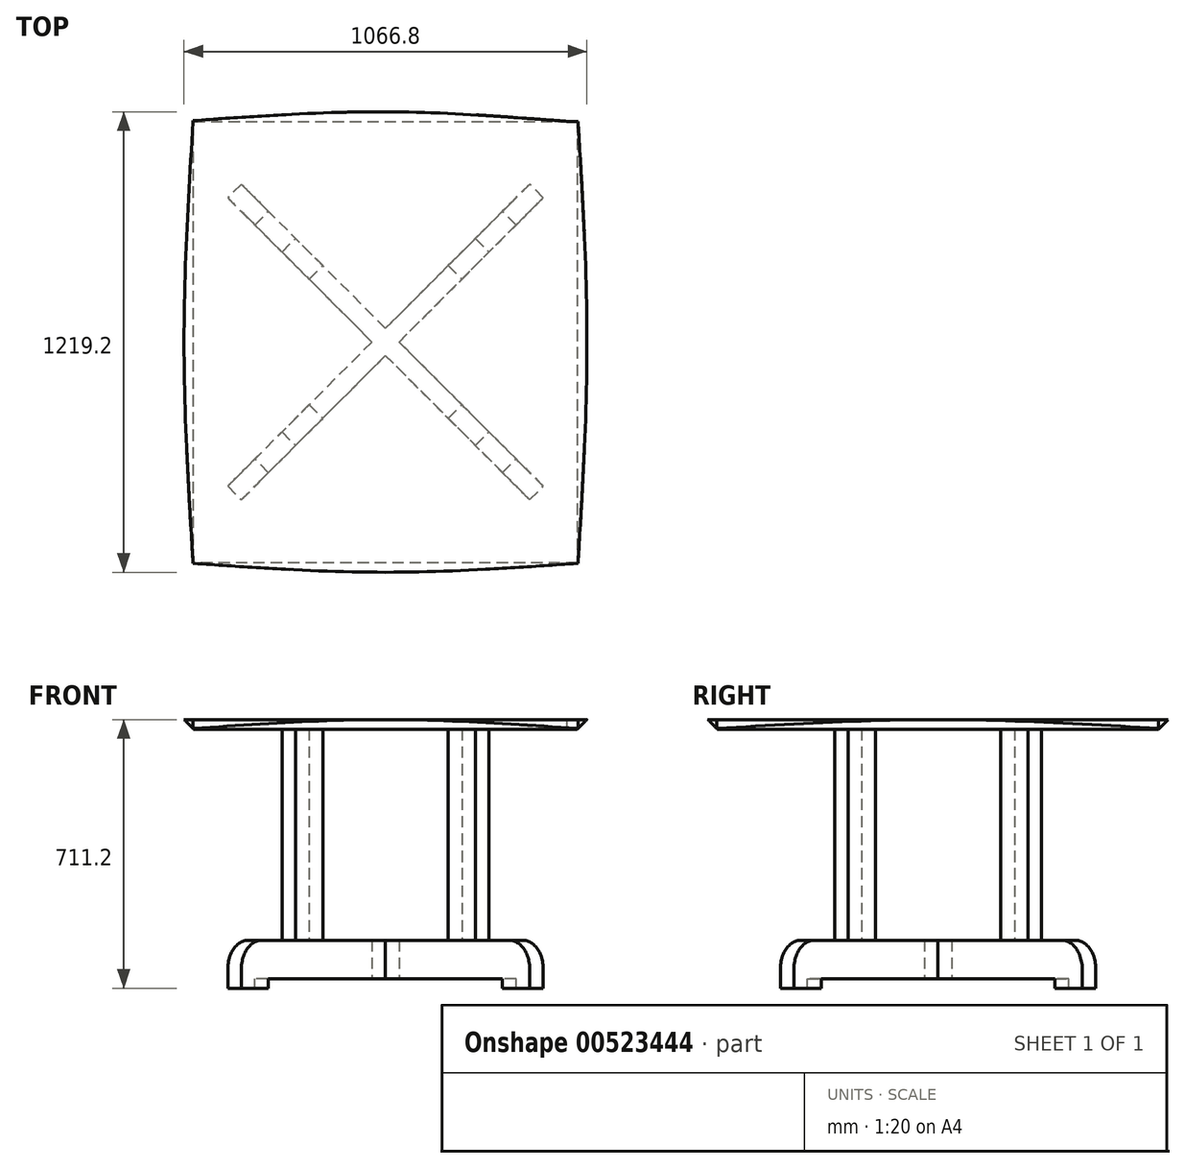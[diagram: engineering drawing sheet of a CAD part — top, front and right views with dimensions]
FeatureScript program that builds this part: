
annotation { "Feature Type Name" : "Feature", "Feature Type Description" : "" }
export const myFeature = defineFeature(function(context is Context, id is Id, definition is map)
    precondition{}
    {
        {
            var Q0;
            Q0=qCreatedBy(makeId("Top.planeOp"),FACE);
            var sketch = newSketch(context, id + "F0", { "sketchPlane" : qUnion([Q0])});
            skLineSegment(sketch, "E0.bottom", {"start": v(-533.4, 609.6) * mm, "end": v(533.4, 609.6) * mm});
            skLineSegment(sketch, "E0.top", {"start": v(-533.4, -609.6) * mm, "end": v(533.4, -609.6) * mm});
            skLineSegment(sketch, "E0.left", {"start": v(-533.4, 609.6) * mm, "end": v(-533.4, -609.6) * mm});
            skLineSegment(sketch, "E0.right", {"start": v(533.4, 609.6) * mm, "end": v(533.4, -609.6) * mm});
            skPoint(sketch, "E1.visualSharp", {"position": v(-533.4, 609.6) * mm});
            skPoint(sketch, "E2.visualSharp", {"position": v(533.4, 609.6) * mm});
            skPoint(sketch, "E3.visualSharp", {"position": v(533.4, -609.6) * mm});
            skPoint(sketch, "E4.visualSharp", {"position": v(-533.4, -609.6) * mm});
            skSolve(sketch);
        }
        {
            var Q0;
            Q0=makeQuery(id+"F0.imprint","IMPRINT",FACE,{"disambiguationData":[TD([[makeQuery(id+"F0.imprint","IMPRINT",EDGE,{"derivedFrom":sQuery(id+"F0.wireOp",EDGE,"E0.bottom")}),-1.0]])]});
            extrude(context, id + "F1", {"entities" : qUnion([Q0]), "depth" : 25.4 * mm, "offsetDistance" : 25.4 * mm});
        }
        {
            var Q0;
            Q0=makeQuery(id+"F1.opExtrude","CAP_EDGE",EDGE,{"disambiguationData":[OSD([sQuery(id+"F0.wireOp",EDGE,"E0.right")])],"isStart":true});
            var Q1;
            Q1=makeQuery(id+"F1.opExtrude","CAP_EDGE",EDGE,{"disambiguationData":[OSD([sQuery(id+"F0.wireOp",EDGE,"E0.top")])],"isStart":true});
            var Q2;
            Q2=makeQuery(id+"F1.opExtrude","CAP_EDGE",EDGE,{"disambiguationData":[OSD([sQuery(id+"F0.wireOp",EDGE,"E0.left")])],"isStart":true});
            var Q3;
            Q3=makeQuery(id+"F1.opExtrude","CAP_EDGE",EDGE,{"disambiguationData":[OSD([sQuery(id+"F0.wireOp",EDGE,"E0.bottom")])],"isStart":true});
            chamfer(context, id + "F2", {"entities" : qUnion([Q0, Q1, Q2, Q3]), "width" : 25.4 * mm, "tangentPropagation" : true});
        }
        {
            var Q0;
            Q0=makeQuery(id+"F1.opExtrude","CAP_FACE",FACE,{"disambiguationData":[OSD([sQuery(id+"F0.wireOp",EDGE,"E0.bottom"),sQuery(id+"F0.wireOp",EDGE,"E0.top"),sQuery(id+"F0.wireOp",EDGE,"E0.left"),sQuery(id+"F0.wireOp",EDGE,"E0.right")])],"isStart":false});
            var sketch = newSketch(context, id + "F3", { "sketchPlane" : qUnion([Q0])});
            skLineSegment(sketch, "E5.0", {"start": v(-533.4, -584.2) * mm, "end": v(533.4, -584.2) * mm});
            skLineSegment(sketch, "E5.1", {"start": v(508, 609.6) * mm, "end": v(508, -609.6) * mm});
            skLineSegment(sketch, "E6.0", {"start": v(-533.4, 584.2) * mm, "end": v(533.4, 584.2) * mm});
            skLineSegment(sketch, "E6.1", {"start": v(-508, 609.6) * mm, "end": v(-508, -609.6) * mm});
            skLineSegment(sketch, "E7.0", {"start": v(-533.4, -609.6) * mm, "end": v(533.4, -609.6) * mm});
            skLineSegment(sketch, "E8.0", {"start": v(-533.4, 609.6) * mm, "end": v(-533.4, -609.6) * mm});
            skLineSegment(sketch, "E9.0", {"start": v(-533.4, 609.6) * mm, "end": v(533.4, 609.6) * mm});
            skLineSegment(sketch, "E10.0", {"start": v(533.4, 609.6) * mm, "end": v(533.4, -609.6) * mm});
            skFitSpline(sketch, "E11", {"points": [v(508, -609.6) * mm, v(533.4, 0) * mm, v(508, 609.6) * mm], "startDerivative": vector(76.2, 1219.2) * mm, "endDerivative": vector(-76.2, 1219.2) * mm});
            skFitSpline(sketch, "E12", {"points": [v(-508, -609.6) * mm, v(-533.4, 0) * mm, v(-508, 609.6) * mm], "startDerivative": vector(-76.2, 1219.2) * mm, "endDerivative": vector(76.2, 1219.2) * mm});
            skFitSpline(sketch, "E13", {"points": [v(-533.4, -584.2) * mm, v(0, -609.6) * mm, v(533.4, -584.2) * mm], "startDerivative": vector(1066.8, -76.2) * mm, "endDerivative": vector(1066.8, 76.2) * mm});
            skFitSpline(sketch, "E14", {"points": [v(-533.4, 584.2) * mm, v(0, 609.6) * mm, v(480.85, 584.2) * mm], "startDerivative": vector(1066.8, 76.2) * mm, "endDerivative": vector(1066.8, -76.2) * mm});
            skSolve(sketch);
        }
        {
            var Q0;
            {var subQ0=sQuery(id+"F3.wireOp",EDGE,"E7.0");var subQ3=sQuery(id+"F3.wireOp",EDGE,"E13");var subQ5=makeQuery(id+"F3.imprint","INTERSECT",VERTEX,{"derivedFrom":[subQ0,subQ3]});Q0=makeQuery(id+"F3.imprint","IMPRINT",FACE,{"disambiguationData":[TD([[makeQuery(id+"F3.imprint","IMPRINT",EDGE,{"disambiguationData":[TD([[subQ5,1.0]])],"derivedFrom":subQ3}),-1.0]])]});}
            var Q1;
            {var subQ0=sQuery(id+"F3.wireOp",EDGE,"E8.0");var subQ1=sQuery(id+"F3.wireOp",EDGE,"E7.0");var subQ2=makeQuery(id+"F3.imprint","INTERSECT",VERTEX,{"derivedFrom":[subQ1,subQ0]});Q1=makeQuery(id+"F3.imprint","IMPRINT",FACE,{"disambiguationData":[TD([[makeQuery(id+"F3.imprint","IMPRINT",EDGE,{"disambiguationData":[TD([[subQ2,-1.0]])],"derivedFrom":subQ1}),1.0]])]});}
            var Q2;
            {var subQ0=sQuery(id+"F3.wireOp",EDGE,"E8.0");var subQ3=sQuery(id+"F3.wireOp",EDGE,"E12");var subQ5=makeQuery(id+"F3.imprint","INTERSECT",VERTEX,{"derivedFrom":[subQ0,subQ3]});Q2=makeQuery(id+"F3.imprint","IMPRINT",FACE,{"disambiguationData":[TD([[makeQuery(id+"F3.imprint","IMPRINT",EDGE,{"disambiguationData":[TD([[subQ5,1.0]])],"derivedFrom":subQ3}),1.0]])]});}
            var Q3;
            {var subQ0=sQuery(id+"F3.wireOp",EDGE,"E8.0");var subQ3=sQuery(id+"F3.wireOp",EDGE,"E12");var subQ5=makeQuery(id+"F3.imprint","INTERSECT",VERTEX,{"derivedFrom":[subQ0,subQ3]});Q3=makeQuery(id+"F3.imprint","IMPRINT",FACE,{"disambiguationData":[TD([[makeQuery(id+"F3.imprint","IMPRINT",EDGE,{"disambiguationData":[TD([[subQ5,-1.0]])],"derivedFrom":subQ3}),1.0]])]});}
            var Q4;
            {var subQ0=sQuery(id+"F3.wireOp",EDGE,"E9.0");var subQ1=sQuery(id+"F3.wireOp",EDGE,"E8.0");var subQ2=makeQuery(id+"F3.imprint","INTERSECT",VERTEX,{"derivedFrom":[subQ1,subQ0]});Q4=makeQuery(id+"F3.imprint","IMPRINT",FACE,{"disambiguationData":[TD([[makeQuery(id+"F3.imprint","IMPRINT",EDGE,{"disambiguationData":[TD([[subQ2,-1.0]])],"derivedFrom":subQ1}),1.0]])]});}
            var Q5;
            {var subQ0=sQuery(id+"F3.wireOp",EDGE,"E9.0");var subQ3=sQuery(id+"F3.wireOp",EDGE,"E14");var subQ5=makeQuery(id+"F3.imprint","INTERSECT",VERTEX,{"derivedFrom":[subQ0,subQ3]});Q5=makeQuery(id+"F3.imprint","IMPRINT",FACE,{"disambiguationData":[TD([[makeQuery(id+"F3.imprint","IMPRINT",EDGE,{"disambiguationData":[TD([[subQ5,1.0]])],"derivedFrom":subQ3}),1.0]])]});}
            var Q6;
            {var subQ0=sQuery(id+"F3.wireOp",EDGE,"E9.0");var subQ3=sQuery(id+"F3.wireOp",EDGE,"E14");var subQ5=makeQuery(id+"F3.imprint","INTERSECT",VERTEX,{"derivedFrom":[subQ0,subQ3]});Q6=makeQuery(id+"F3.imprint","IMPRINT",FACE,{"disambiguationData":[TD([[makeQuery(id+"F3.imprint","IMPRINT",EDGE,{"disambiguationData":[TD([[subQ5,-1.0]])],"derivedFrom":subQ3}),1.0]])]});}
            var Q7;
            {var subQ0=sQuery(id+"F3.wireOp",EDGE,"E10.0");var subQ1=sQuery(id+"F3.wireOp",EDGE,"E9.0");var subQ2=makeQuery(id+"F3.imprint","INTERSECT",VERTEX,{"derivedFrom":[subQ1,subQ0]});Q7=makeQuery(id+"F3.imprint","IMPRINT",FACE,{"disambiguationData":[TD([[makeQuery(id+"F3.imprint","IMPRINT",EDGE,{"disambiguationData":[TD([[subQ2,1.0]])],"derivedFrom":subQ1}),-1.0]])]});}
            var Q8;
            {var subQ0=sQuery(id+"F3.wireOp",EDGE,"E10.0");var subQ3=sQuery(id+"F3.wireOp",EDGE,"E11");var subQ5=makeQuery(id+"F3.imprint","INTERSECT",VERTEX,{"derivedFrom":[subQ0,subQ3]});Q8=makeQuery(id+"F3.imprint","IMPRINT",FACE,{"disambiguationData":[TD([[makeQuery(id+"F3.imprint","IMPRINT",EDGE,{"disambiguationData":[TD([[subQ5,-1.0]])],"derivedFrom":subQ3}),-1.0]])]});}
            var Q9;
            {var subQ0=sQuery(id+"F3.wireOp",EDGE,"E10.0");var subQ3=sQuery(id+"F3.wireOp",EDGE,"E11");var subQ5=makeQuery(id+"F3.imprint","INTERSECT",VERTEX,{"derivedFrom":[subQ0,subQ3]});Q9=makeQuery(id+"F3.imprint","IMPRINT",FACE,{"disambiguationData":[TD([[makeQuery(id+"F3.imprint","IMPRINT",EDGE,{"disambiguationData":[TD([[subQ5,1.0]])],"derivedFrom":subQ3}),-1.0]])]});}
            var Q10;
            {var subQ0=sQuery(id+"F3.wireOp",EDGE,"E10.0");var subQ1=sQuery(id+"F3.wireOp",EDGE,"E7.0");var subQ2=makeQuery(id+"F3.imprint","INTERSECT",VERTEX,{"derivedFrom":[subQ1,subQ0]});Q10=makeQuery(id+"F3.imprint","IMPRINT",FACE,{"disambiguationData":[TD([[makeQuery(id+"F3.imprint","IMPRINT",EDGE,{"disambiguationData":[TD([[subQ2,1.0]])],"derivedFrom":subQ1}),1.0]])]});}
            var Q11;
            {var subQ0=sQuery(id+"F3.wireOp",EDGE,"E7.0");var subQ3=sQuery(id+"F3.wireOp",EDGE,"E13");var subQ5=makeQuery(id+"F3.imprint","INTERSECT",VERTEX,{"derivedFrom":[subQ0,subQ3]});Q11=makeQuery(id+"F3.imprint","IMPRINT",FACE,{"disambiguationData":[TD([[makeQuery(id+"F3.imprint","IMPRINT",EDGE,{"disambiguationData":[TD([[subQ5,-1.0]])],"derivedFrom":subQ3}),-1.0]])]});}
            var Q12;
            {var subQ1=sQuery(id+"F3.wireOp",EDGE,"E6.0");var subQ3=sQuery(id+"F3.wireOp",EDGE,"E11");var subQ4=makeQuery(id+"F3.imprint","INTERSECT",VERTEX,{"derivedFrom":[subQ1,subQ3]});Q12=makeQuery(id+"F3.imprint","IMPRINT",FACE,{"disambiguationData":[TD([[makeQuery(id+"F3.imprint","IMPRINT",EDGE,{"disambiguationData":[TD([[subQ4,-1.0]])],"derivedFrom":subQ3}),-1.0]])]});}
            var Q13;
            {var subQ1=sQuery(id+"F3.wireOp",EDGE,"E5.1");var subQ3=sQuery(id+"F3.wireOp",EDGE,"E14");var subQ4=makeQuery(id+"F3.imprint","INTERSECT",VERTEX,{"derivedFrom":[subQ1,subQ3]});Q13=makeQuery(id+"F3.imprint","IMPRINT",FACE,{"disambiguationData":[TD([[makeQuery(id+"F3.imprint","IMPRINT",EDGE,{"disambiguationData":[TD([[subQ4,-1.0]])],"derivedFrom":subQ3}),1.0]])]});}
            var Q14;
            {var subQ1=sQuery(id+"F3.wireOp",EDGE,"E5.0");var subQ3=sQuery(id+"F3.wireOp",EDGE,"E11");var subQ4=makeQuery(id+"F3.imprint","INTERSECT",VERTEX,{"derivedFrom":[subQ1,subQ3]});Q14=makeQuery(id+"F3.imprint","IMPRINT",FACE,{"disambiguationData":[TD([[makeQuery(id+"F3.imprint","IMPRINT",EDGE,{"disambiguationData":[TD([[subQ4,1.0]])],"derivedFrom":subQ3}),-1.0]])]});}
            var Q15;
            {var subQ1=sQuery(id+"F3.wireOp",EDGE,"E5.1");var subQ3=sQuery(id+"F3.wireOp",EDGE,"E13");var subQ4=makeQuery(id+"F3.imprint","INTERSECT",VERTEX,{"derivedFrom":[subQ1,subQ3]});Q15=makeQuery(id+"F3.imprint","IMPRINT",FACE,{"disambiguationData":[TD([[makeQuery(id+"F3.imprint","IMPRINT",EDGE,{"disambiguationData":[TD([[subQ4,-1.0]])],"derivedFrom":subQ3}),-1.0]])]});}
            var Q16;
            {var subQ1=sQuery(id+"F3.wireOp",EDGE,"E5.0");var subQ3=sQuery(id+"F3.wireOp",EDGE,"E12");var subQ4=makeQuery(id+"F3.imprint","INTERSECT",VERTEX,{"derivedFrom":[subQ1,subQ3]});Q16=makeQuery(id+"F3.imprint","IMPRINT",FACE,{"disambiguationData":[TD([[makeQuery(id+"F3.imprint","IMPRINT",EDGE,{"disambiguationData":[TD([[subQ4,1.0]])],"derivedFrom":subQ3}),1.0]])]});}
            var Q17;
            {var subQ1=sQuery(id+"F3.wireOp",EDGE,"E6.1");var subQ3=sQuery(id+"F3.wireOp",EDGE,"E13");var subQ4=makeQuery(id+"F3.imprint","INTERSECT",VERTEX,{"derivedFrom":[subQ1,subQ3]});Q17=makeQuery(id+"F3.imprint","IMPRINT",FACE,{"disambiguationData":[TD([[makeQuery(id+"F3.imprint","IMPRINT",EDGE,{"disambiguationData":[TD([[subQ4,1.0]])],"derivedFrom":subQ3}),-1.0]])]});}
            var Q18;
            {var subQ1=sQuery(id+"F3.wireOp",EDGE,"E6.1");var subQ3=sQuery(id+"F3.wireOp",EDGE,"E14");var subQ4=makeQuery(id+"F3.imprint","INTERSECT",VERTEX,{"derivedFrom":[subQ1,subQ3]});Q18=makeQuery(id+"F3.imprint","IMPRINT",FACE,{"disambiguationData":[TD([[makeQuery(id+"F3.imprint","IMPRINT",EDGE,{"disambiguationData":[TD([[subQ4,1.0]])],"derivedFrom":subQ3}),1.0]])]});}
            var Q19;
            {var subQ1=sQuery(id+"F3.wireOp",EDGE,"E6.0");var subQ3=sQuery(id+"F3.wireOp",EDGE,"E12");var subQ4=makeQuery(id+"F3.imprint","INTERSECT",VERTEX,{"derivedFrom":[subQ1,subQ3]});Q19=makeQuery(id+"F3.imprint","IMPRINT",FACE,{"disambiguationData":[TD([[makeQuery(id+"F3.imprint","IMPRINT",EDGE,{"disambiguationData":[TD([[subQ4,-1.0]])],"derivedFrom":subQ3}),1.0]])]});}
            var Q20;
            {var subQ1=sQuery(id+"F3.wireOp",EDGE,"E5.1");var subQ3=sQuery(id+"F3.wireOp",EDGE,"E6.0");var subQ4=makeQuery(id+"F3.imprint","INTERSECT",VERTEX,{"derivedFrom":[subQ1,subQ3]});Q20=makeQuery(id+"F3.imprint","IMPRINT",FACE,{"disambiguationData":[TD([[makeQuery(id+"F3.imprint","IMPRINT",EDGE,{"disambiguationData":[TD([[subQ4,-1.0]])],"derivedFrom":subQ3}),1.0]])]});}
            extrude(context, id + "F4", {"entities" : qUnion([Q0, Q1, Q2, Q3, Q4, Q5, Q6, Q7, Q8, Q9, Q10, Q11, Q12, Q13, Q14, Q15, Q16, Q17, Q18, Q19, Q20]), "operationType" : NewBodyOperationType.REMOVE, "oppositeDirection" : true, "depth" : 25.4 * mm, "offsetDistance" : 25.4 * mm});
        }
        {
            var Q0;
            Q0=makeQuery(id+"F1.opExtrude","CAP_FACE",FACE,{"disambiguationData":[OSD([sQuery(id+"F0.wireOp",EDGE,"E0.bottom"),sQuery(id+"F0.wireOp",EDGE,"E0.top"),sQuery(id+"F0.wireOp",EDGE,"E0.left"),sQuery(id+"F0.wireOp",EDGE,"E0.right")])],"isStart":false});
            cPlane(context, id + "F5", {"entities" : qUnion([Q0]), "cplaneType" : CPlaneType.OFFSET, "offset" : 711.2 * mm, "oppositeDirection" : true, "width" : 152.4 * mm, "height" : 152.4 * mm});
        }
        {
            var Q0;
            Q0=qCreatedBy(id+"F5.planeOp",FACE);
            var sketch = newSketch(context, id + "F6", { "sketchPlane" : qUnion([Q0])});
            skFitSpline(sketch, "E15.0.0", {"points": [v(-533.4, -584.2) * mm, v(-355.6, -596.9) * mm, v(0, -622.3) * mm, v(355.6, -596.9) * mm, v(533.4, -584.2) * mm]});
            skFitSpline(sketch, "E15.0.1", {"points": [v(508, -609.6) * mm, v(520.7, -406.4) * mm, v(546.1, 0) * mm, v(520.7, 406.4) * mm, v(508, 609.6) * mm]});
            skFitSpline(sketch, "E15.0.2", {"points": [v(508, -609.6) * mm, v(520.7, -406.4) * mm, v(546.1, 0) * mm, v(520.7, 406.4) * mm, v(508, 609.6) * mm]});
            skLineSegment(sketch, "E15.0.3", {"start": v(509.59, 584.2) * mm, "end": v(480.85, 584.2) * mm});
            skFitSpline(sketch, "E15.0.4", {"points": [v(480.85, 584.2) * mm, v(307.65, 596.57) * mm, v(4.66, 622.33) * mm, v(-351, 597.23) * mm, v(-533.4, 584.2) * mm]});
            skLineSegment(sketch, "E15.0.5", {"start": v(0, 609.6) * mm, "end": v(-19.42, 609.6) * mm});
            skFitSpline(sketch, "E15.0.6", {"points": [v(480.85, 584.2) * mm, v(307.65, 596.57) * mm, v(4.66, 622.33) * mm, v(-351, 597.23) * mm, v(-533.4, 584.2) * mm]});
            skFitSpline(sketch, "E15.0.7", {"points": [v(-508, 609.6) * mm, v(-520.7, 406.4) * mm, v(-546.1, 0) * mm, v(-520.7, -406.4) * mm, v(-508, -609.6) * mm]});
            skFitSpline(sketch, "E15.0.8", {"points": [v(-508, 609.6) * mm, v(-520.7, 406.4) * mm, v(-546.1, 0) * mm, v(-520.7, -406.4) * mm, v(-508, -609.6) * mm]});
            skFitSpline(sketch, "E15.0.9", {"points": [v(-533.4, -584.2) * mm, v(-355.6, -596.9) * mm, v(0, -622.3) * mm, v(355.6, -596.9) * mm, v(533.4, -584.2) * mm]});
            skLineSegment(sketch, "E16", {"start": v(-381.66, -417.58) * mm, "end": v(417.58, 381.66) * mm});
            skLineSegment(sketch, "E17", {"start": v(-417.58, 381.66) * mm, "end": v(381.66, -417.58) * mm});
            skLineSegment(sketch, "E18", {"start": v(381.66, -417.58) * mm, "end": v(417.58, -381.66) * mm});
            skLineSegment(sketch, "E19", {"start": v(417.58, -381.66) * mm, "end": v(-381.66, 417.58) * mm});
            skLineSegment(sketch, "E20", {"start": v(-381.66, 417.58) * mm, "end": v(-417.58, 381.66) * mm});
            skLineSegment(sketch, "E21", {"start": v(417.58, 381.66) * mm, "end": v(381.66, 417.58) * mm});
            skLineSegment(sketch, "E22", {"start": v(381.66, 417.58) * mm, "end": v(-417.58, -381.66) * mm});
            skLineSegment(sketch, "E23", {"start": v(-417.58, -381.66) * mm, "end": v(-381.66, -417.58) * mm});
            skLineSegment(sketch, "E24", {"start": v(0, 0) * mm, "end": v(0, -609.6) * mm, "construction": true});
            skLineSegment(sketch, "E25", {"start": v(0, 0) * mm, "end": v(509.48, -585.9) * mm, "construction": true});
            skLineSegment(sketch, "E26", {"start": v(0, 0) * mm, "end": v(-509.48, -585.9) * mm, "construction": true});
            skSolve(sketch);
        }
        {
            var Q0;
            {var subQ0=sQuery(id+"F6.wireOp",EDGE,"E23");Q0=makeQuery(id+"F6.imprint","IMPRINT",FACE,{"disambiguationData":[TD([[makeQuery(id+"F6.imprint","IMPRINT",EDGE,{"derivedFrom":subQ0}),1.0]])]});}
            var Q1;
            {var subQ0=sQuery(id+"F6.wireOp",EDGE,"E17");var subQ1=sQuery(id+"F6.wireOp",EDGE,"E16");var subQ2=makeQuery(id+"F6.imprint","INTERSECT",VERTEX,{"derivedFrom":[subQ1,subQ0]});Q1=makeQuery(id+"F6.imprint","IMPRINT",FACE,{"disambiguationData":[TD([[makeQuery(id+"F6.imprint","IMPRINT",EDGE,{"disambiguationData":[TD([[subQ2,-1.0]])],"derivedFrom":subQ1}),1.0]])]});}
            var Q2;
            {var subQ0=sQuery(id+"F6.wireOp",EDGE,"E21");Q2=makeQuery(id+"F6.imprint","IMPRINT",FACE,{"disambiguationData":[TD([[makeQuery(id+"F6.imprint","IMPRINT",EDGE,{"derivedFrom":subQ0}),1.0]])]});}
            var Q3;
            {var subQ5=sQuery(id+"F6.wireOp",EDGE,"E18");Q3=makeQuery(id+"F6.imprint","IMPRINT",FACE,{"disambiguationData":[TD([[makeQuery(id+"F6.imprint","IMPRINT",EDGE,{"derivedFrom":subQ5}),1.0]])]});}
            var Q4;
            {var subQ0=sQuery(id+"F6.wireOp",EDGE,"E20");Q4=makeQuery(id+"F6.imprint","IMPRINT",FACE,{"disambiguationData":[TD([[makeQuery(id+"F6.imprint","IMPRINT",EDGE,{"derivedFrom":subQ0}),1.0]])]});}
            extrude(context, id + "F7", {"entities" : qUnion([Q0, Q1, Q2, Q3, Q4]), "depth" : 127 * mm, "offsetDistance" : 25.4 * mm});
        }
        {
            var Q0;
            {var subQ0=sQuery(id+"F6.wireOp",EDGE,"E19");Q0=makeQuery(id+"F7.opExtrude","SWEPT_FACE",FACE,{"disambiguationData":[OSD([subQ0]),TDD([makeQuery(id+"F6.imprint","IMPRINT",EDGE,{"disambiguationData":[TD([[makeQuery(id+"F6.imprint","INTERSECT",VERTEX,{"derivedFrom":[sQuery(id+"F6.wireOp",EDGE,"E18"),subQ0]}),-1.0]])],"derivedFrom":subQ0})])]});}
            var sketch = newSketch(context, id + "F8", { "sketchPlane" : qUnion([Q0])});
            skLineSegment(sketch, "E27.0.0", {"start": v(-565.15, -685.8) * mm, "end": v(-25.4, -685.8) * mm});
            skLineSegment(sketch, "E27.0.1", {"start": v(-25.4, -685.8) * mm, "end": v(-25.4, -558.8) * mm});
            skLineSegment(sketch, "E27.0.2", {"start": v(-25.4, -558.8) * mm, "end": v(-488.95, -558.8) * mm});
            skLineSegment(sketch, "E27.0.3", {"start": v(-565.15, -635) * mm, "end": v(-565.15, -685.8) * mm});
            skLineSegment(sketch, "E28.0.0", {"start": v(25.4, -685.8) * mm, "end": v(565.15, -685.8) * mm});
            skLineSegment(sketch, "E28.0.1", {"start": v(565.15, -685.8) * mm, "end": v(565.15, -635) * mm});
            skLineSegment(sketch, "E28.0.2", {"start": v(488.95, -558.8) * mm, "end": v(25.4, -558.8) * mm});
            skLineSegment(sketch, "E28.0.3", {"start": v(25.4, -558.8) * mm, "end": v(25.4, -685.8) * mm});
            skPoint(sketch, "E29.oppositeSnap0", {"position": v(-571.5, -660.4) * mm});
            skLineSegment(sketch, "E29.bottom", {"start": v(-463.55, -685.8) * mm, "end": v(463.55, -685.8) * mm});
            skLineSegment(sketch, "E29.top", {"start": v(-463.55, -660.4) * mm, "end": v(463.55, -660.4) * mm});
            skLineSegment(sketch, "E29.left", {"start": v(-463.55, -685.8) * mm, "end": v(-463.55, -660.4) * mm});
            skLineSegment(sketch, "E29.right", {"start": v(463.55, -685.8) * mm, "end": v(463.55, -660.4) * mm});
            skPoint(sketch, "E30.visualSharp", {"position": v(-565.15, -558.8) * mm});
            skArc(sketch, "E30.filletArc", {"start": v(-488.95, -558.8) * mm, "mid": v(-542.83, -581.12) * mm, "end": v(-565.15, -635) * mm});
            skPoint(sketch, "E31.visualSharp", {"position": v(565.15, -558.8) * mm});
            skArc(sketch, "E31.filletArc", {"start": v(565.15, -635) * mm, "mid": v(542.83, -581.12) * mm, "end": v(488.95, -558.8) * mm});
            skLineSegment(sketch, "E32.0", {"start": v(565.15, -558.8) * mm, "end": v(565.15, -685.8) * mm});
            skLineSegment(sketch, "E33.0", {"start": v(25.4, -558.8) * mm, "end": v(565.15, -558.8) * mm});
            skSolve(sketch);
        }
        {
            var Q0;
            {var subQ0=sQuery(id+"F8.wireOp",EDGE,"E30.filletArc");Q0=makeQuery(id+"F8.imprint","IMPRINT",FACE,{"disambiguationData":[TD([[makeQuery(id+"F8.imprint","IMPRINT",EDGE,{"derivedFrom":subQ0}),-1.0]])]});}
            var Q1;
            {var subQ5=sQuery(id+"F8.wireOp",EDGE,"E29.left");Q1=makeQuery(id+"F8.imprint","IMPRINT",FACE,{"disambiguationData":[TD([[makeQuery(id+"F8.imprint","IMPRINT",EDGE,{"derivedFrom":subQ5}),-1.0]])]});}
            var Q2;
            {var subQ5=sQuery(id+"F8.wireOp",EDGE,"E29.right");Q2=makeQuery(id+"F8.imprint","IMPRINT",FACE,{"disambiguationData":[TD([[makeQuery(id+"F8.imprint","IMPRINT",EDGE,{"derivedFrom":subQ5}),1.0]])]});}
            var Q3;
            {var subQ0=sQuery(id+"F8.wireOp",EDGE,"E29.bottom");var subQ1=sQuery(id+"F8.wireOp",EDGE,"E27.0.1");var subQ2=makeQuery(id+"F8.imprint","INTERSECT",VERTEX,{"derivedFrom":[subQ1,subQ0]});Q3=makeQuery(id+"F8.imprint","IMPRINT",FACE,{"disambiguationData":[TD([[makeQuery(id+"F8.imprint","IMPRINT",EDGE,{"disambiguationData":[TD([[subQ2,1.0]])],"derivedFrom":subQ1}),1.0]])]});}
            var Q4;
            {var subQ0=sQuery(id+"F8.wireOp",EDGE,"E31.filletArc");Q4=makeQuery(id+"F8.imprint","IMPRINT",FACE,{"disambiguationData":[TD([[makeQuery(id+"F8.imprint","IMPRINT",EDGE,{"derivedFrom":subQ0}),-1.0]])]});}
            extrude(context, id + "F9", {"entities" : qUnion([Q0, Q1, Q2, Q3, Q4]), "operationType" : NewBodyOperationType.REMOVE, "oppositeDirection" : true, "depth" : 50.8 * mm, "offsetDistance" : 25.4 * mm});
        }
        {
            var Q0;
            {var subQ0=sQuery(id+"F6.wireOp",EDGE,"E22");Q0=makeQuery(id+"F7.opExtrude","SWEPT_FACE",FACE,{"disambiguationData":[OSD([subQ0]),TDD([makeQuery(id+"F6.imprint","IMPRINT",EDGE,{"disambiguationData":[TD([[makeQuery(id+"F6.imprint","INTERSECT",VERTEX,{"derivedFrom":[sQuery(id+"F6.wireOp",EDGE,"E21"),subQ0]}),-1.0]])],"derivedFrom":subQ0})])]});}
            var sketch = newSketch(context, id + "F10", { "sketchPlane" : qUnion([Q0])});
            skLineSegment(sketch, "E34.0.0", {"start": v(-565.15, -685.8) * mm, "end": v(-25.4, -685.8) * mm});
            skLineSegment(sketch, "E34.0.1", {"start": v(-25.4, -685.8) * mm, "end": v(-25.4, -660.4) * mm});
            skLineSegment(sketch, "E34.0.2", {"start": v(-25.4, -660.4) * mm, "end": v(-25.4, -558.8) * mm});
            skLineSegment(sketch, "E34.0.3", {"start": v(-25.4, -558.8) * mm, "end": v(-488.95, -558.8) * mm});
            skLineSegment(sketch, "E34.0.4", {"start": v(-565.15, -635) * mm, "end": v(-565.15, -685.8) * mm});
            skLineSegment(sketch, "E35.0.0", {"start": v(25.4, -685.8) * mm, "end": v(565.15, -685.8) * mm});
            skLineSegment(sketch, "E35.0.1", {"start": v(565.15, -685.8) * mm, "end": v(565.15, -635) * mm});
            skLineSegment(sketch, "E35.0.2", {"start": v(488.95, -558.8) * mm, "end": v(25.4, -558.8) * mm});
            skLineSegment(sketch, "E35.0.3", {"start": v(25.4, -558.8) * mm, "end": v(25.4, -660.4) * mm});
            skLineSegment(sketch, "E35.0.4", {"start": v(25.4, -660.4) * mm, "end": v(25.4, -685.8) * mm});
            skPoint(sketch, "E36.visualSharp", {"position": v(-565.15, -558.8) * mm});
            skArc(sketch, "E36.filletArc", {"start": v(-488.95, -558.8) * mm, "mid": v(-542.83, -581.12) * mm, "end": v(-565.15, -635) * mm});
            skPoint(sketch, "E37.visualSharp", {"position": v(565.15, -558.8) * mm});
            skArc(sketch, "E37.filletArc", {"start": v(565.15, -635) * mm, "mid": v(542.83, -581.12) * mm, "end": v(488.95, -558.8) * mm});
            skLineSegment(sketch, "E38.bottom", {"start": v(-463.55, -685.8) * mm, "end": v(463.55, -685.8) * mm});
            skLineSegment(sketch, "E38.top", {"start": v(-463.55, -660.4) * mm, "end": v(463.55, -660.4) * mm});
            skLineSegment(sketch, "E38.left", {"start": v(-463.55, -685.8) * mm, "end": v(-463.55, -660.4) * mm});
            skLineSegment(sketch, "E38.right", {"start": v(463.55, -685.8) * mm, "end": v(463.55, -660.4) * mm});
            skLineSegment(sketch, "E39.0", {"start": v(25.4, -558.8) * mm, "end": v(565.15, -558.8) * mm});
            skLineSegment(sketch, "E40.0", {"start": v(565.15, -558.8) * mm, "end": v(565.15, -685.8) * mm});
            skSolve(sketch);
        }
        {
            var Q0;
            {var subQ0=sQuery(id+"F10.wireOp",EDGE,"E36.filletArc");Q0=makeQuery(id+"F10.imprint","IMPRINT",FACE,{"disambiguationData":[TD([[makeQuery(id+"F10.imprint","IMPRINT",EDGE,{"derivedFrom":subQ0}),-1.0]])]});}
            var Q1;
            {var subQ0=sQuery(id+"F10.wireOp",EDGE,"E35.0.4");Q1=makeQuery(id+"F10.imprint","IMPRINT",FACE,{"disambiguationData":[TD([[makeQuery(id+"F10.imprint","IMPRINT",EDGE,{"derivedFrom":subQ0}),1.0]])]});}
            var Q2;
            {var subQ0=sQuery(id+"F10.wireOp",EDGE,"E34.0.1");Q2=makeQuery(id+"F10.imprint","IMPRINT",FACE,{"disambiguationData":[TD([[makeQuery(id+"F10.imprint","IMPRINT",EDGE,{"derivedFrom":subQ0}),-1.0]])]});}
            var Q3;
            {var subQ0=sQuery(id+"F10.wireOp",EDGE,"E37.filletArc");Q3=makeQuery(id+"F10.imprint","IMPRINT",FACE,{"disambiguationData":[TD([[makeQuery(id+"F10.imprint","IMPRINT",EDGE,{"derivedFrom":subQ0}),-1.0]])]});}
            var Q4;
            {var subQ0=sQuery(id+"F10.wireOp",EDGE,"E34.0.1");Q4=makeQuery(id+"F10.imprint","IMPRINT",FACE,{"disambiguationData":[TD([[makeQuery(id+"F10.imprint","IMPRINT",EDGE,{"derivedFrom":subQ0}),1.0]])]});}
            extrude(context, id + "F11", {"entities" : qUnion([Q0, Q1, Q2, Q3, Q4]), "operationType" : NewBodyOperationType.REMOVE, "oppositeDirection" : true, "depth" : 50.8 * mm, "offsetDistance" : 25.4 * mm});
        }
        {
            var Q0;
            Q0=makeQuery(id+"F7.opExtrude","CAP_FACE",FACE,{"disambiguationData":[OSD([sQuery(id+"F6.wireOp",EDGE,"E16"),sQuery(id+"F6.wireOp",EDGE,"E17"),sQuery(id+"F6.wireOp",EDGE,"E18"),sQuery(id+"F6.wireOp",EDGE,"E19"),sQuery(id+"F6.wireOp",EDGE,"E20"),sQuery(id+"F6.wireOp",EDGE,"E21"),sQuery(id+"F6.wireOp",EDGE,"E22"),sQuery(id+"F6.wireOp",EDGE,"E23")])],"isStart":false});
            var sketch = newSketch(context, id + "F12", { "sketchPlane" : qUnion([Q0])});
            skLineSegment(sketch, "E41.0.0", {"start": v(35.92, 0) * mm, "end": v(363.7, 327.78) * mm});
            skLineSegment(sketch, "E41.0.1", {"start": v(363.7, 327.78) * mm, "end": v(327.78, 363.7) * mm});
            skLineSegment(sketch, "E41.0.2", {"start": v(327.78, 363.7) * mm, "end": v(0, 35.92) * mm});
            skLineSegment(sketch, "E41.0.3", {"start": v(0, 35.92) * mm, "end": v(-327.78, 363.7) * mm});
            skLineSegment(sketch, "E41.0.4", {"start": v(-327.78, 363.7) * mm, "end": v(-363.7, 327.78) * mm});
            skLineSegment(sketch, "E41.0.5", {"start": v(-363.7, 327.78) * mm, "end": v(-35.92, 0) * mm});
            skLineSegment(sketch, "E41.0.6", {"start": v(-35.92, 0) * mm, "end": v(-363.7, -327.78) * mm});
            skLineSegment(sketch, "E41.0.7", {"start": v(-363.7, -327.78) * mm, "end": v(-327.78, -363.7) * mm});
            skLineSegment(sketch, "E41.0.8", {"start": v(-327.78, -363.7) * mm, "end": v(0, -35.92) * mm});
            skLineSegment(sketch, "E41.0.9", {"start": v(0, -35.92) * mm, "end": v(327.78, -363.7) * mm});
            skLineSegment(sketch, "E41.0.10", {"start": v(327.78, -363.7) * mm, "end": v(363.7, -327.78) * mm});
            skLineSegment(sketch, "E41.0.11", {"start": v(363.7, -327.78) * mm, "end": v(35.92, 0) * mm});
            skLineSegment(sketch, "E42", {"start": v(-273.9, 237.98) * mm, "end": v(-237.98, 273.9) * mm});
            skLineSegment(sketch, "E43", {"start": v(-202.06, 166.13) * mm, "end": v(-166.13, 202.06) * mm});
            skLineSegment(sketch, "E44", {"start": v(237.98, 273.9) * mm, "end": v(273.9, 237.98) * mm});
            skLineSegment(sketch, "E45", {"start": v(166.13, 202.06) * mm, "end": v(202.06, 166.13) * mm});
            skLineSegment(sketch, "E46", {"start": v(166.13, -202.06) * mm, "end": v(202.06, -166.13) * mm});
            skLineSegment(sketch, "E47", {"start": v(237.98, -273.9) * mm, "end": v(273.9, -237.98) * mm});
            skLineSegment(sketch, "E48", {"start": v(-202.06, -166.13) * mm, "end": v(-166.13, -202.06) * mm});
            skLineSegment(sketch, "E49", {"start": v(-273.9, -237.98) * mm, "end": v(-237.98, -273.9) * mm});
            skLineSegment(sketch, "E50", {"start": v(-237.98, 273.9) * mm, "end": v(-166.13, 202.06) * mm});
            skLineSegment(sketch, "E51", {"start": v(-273.9, 237.98) * mm, "end": v(-202.06, 166.13) * mm});
            skLineSegment(sketch, "E52", {"start": v(166.13, -202.06) * mm, "end": v(237.98, -273.9) * mm});
            skLineSegment(sketch, "E53", {"start": v(202.06, -166.13) * mm, "end": v(273.9, -237.98) * mm});
            skLineSegment(sketch, "E54", {"start": v(237.98, 273.9) * mm, "end": v(166.13, 202.06) * mm});
            skLineSegment(sketch, "E55", {"start": v(273.9, 237.98) * mm, "end": v(202.06, 166.13) * mm});
            skLineSegment(sketch, "E56", {"start": v(-202.06, -166.13) * mm, "end": v(-273.9, -237.98) * mm});
            skLineSegment(sketch, "E57", {"start": v(-166.13, -202.06) * mm, "end": v(-237.98, -273.9) * mm});
            skLineSegment(sketch, "E58.0", {"start": v(-381.66, 417.58) * mm, "end": v(-417.58, 381.66) * mm});
            skLineSegment(sketch, "E59.0", {"start": v(381.66, -417.58) * mm, "end": v(417.58, -381.66) * mm});
            skLineSegment(sketch, "E60.0", {"start": v(-417.58, -381.66) * mm, "end": v(-381.66, -417.58) * mm});
            skLineSegment(sketch, "E61.0", {"start": v(417.58, 381.66) * mm, "end": v(381.66, 417.58) * mm});
            skSolve(sketch);
        }
        {
            var Q0;
            Q0=makeQuery(id+"F12.imprint","IMPRINT",FACE,{"disambiguationData":[TD([[makeQuery(id+"F12.imprint","IMPRINT",EDGE,{"derivedFrom":sQuery(id+"F12.wireOp",EDGE,"E44")}),-1.0]])]});
            var Q1;
            Q1=makeQuery(id+"F12.imprint","IMPRINT",FACE,{"disambiguationData":[TD([[makeQuery(id+"F12.imprint","IMPRINT",EDGE,{"derivedFrom":sQuery(id+"F12.wireOp",EDGE,"E46")}),-1.0]])]});
            var Q2;
            Q2=makeQuery(id+"F12.imprint","IMPRINT",FACE,{"disambiguationData":[TD([[makeQuery(id+"F12.imprint","IMPRINT",EDGE,{"derivedFrom":sQuery(id+"F12.wireOp",EDGE,"E48")}),-1.0]])]});
            var Q3;
            Q3=makeQuery(id+"F12.imprint","IMPRINT",FACE,{"disambiguationData":[TD([[makeQuery(id+"F12.imprint","IMPRINT",EDGE,{"derivedFrom":sQuery(id+"F12.wireOp",EDGE,"E42")}),-1.0]])]});
            extrude(context, id + "F13", {"entities" : qUnion([Q0, Q1, Q2, Q3]), "endBound" : BoundingType.UP_TO_NEXT, "depth" : 25.4 * mm, "offsetDistance" : 25.4 * mm});
        }
    });
